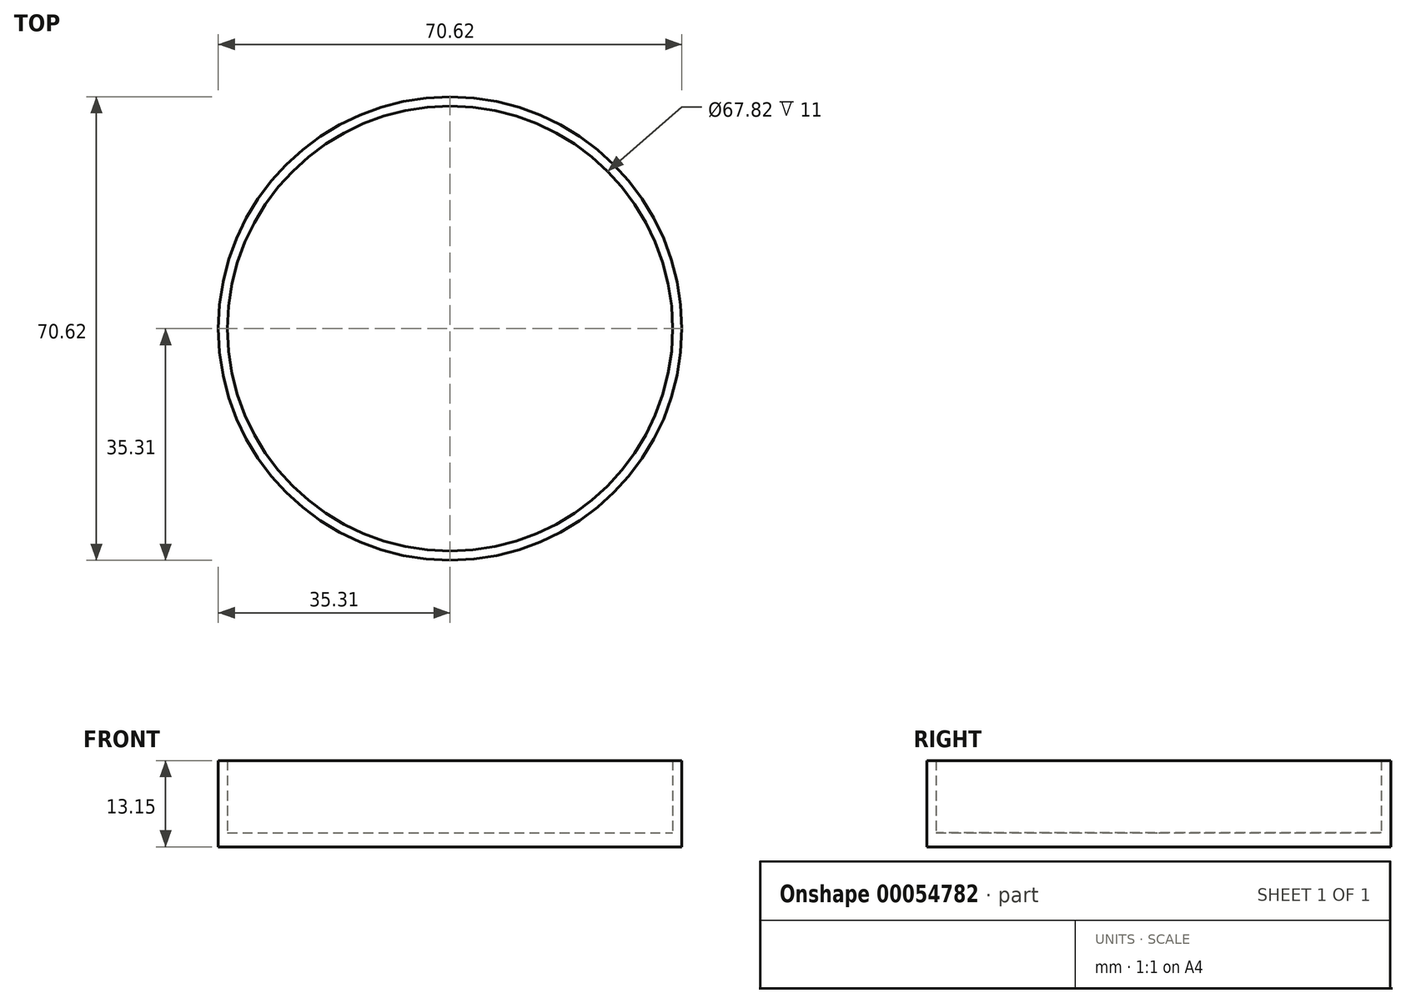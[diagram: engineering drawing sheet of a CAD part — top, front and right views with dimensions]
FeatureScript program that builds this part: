
annotation { "Feature Type Name" : "Feature", "Feature Type Description" : "" }
export const myFeature = defineFeature(function(context is Context, id is Id, definition is map)
    precondition{}
    {
        {
            var Q0;
            Q0=qCreatedBy(makeId("Front.planeOp"),FACE);
            var sketch = newSketch(context, id + "F0", { "sketchPlane" : qUnion([Q0])});
            skLineSegment(sketch, "E0", {"start": v(33.9, 0) * mm, "end": v(33.9, 11) * mm});
            skLineSegment(sketch, "E1", {"start": v(33.9, 0) * mm, "end": v(0, 0) * mm});
            skLineSegment(sketch, "E2", {"start": v(0, 0) * mm, "end": v(0, -2.15) * mm});
            skLineSegment(sketch, "E3", {"start": v(0, -2.15) * mm, "end": v(34.9, -2.15) * mm});
            skLineSegment(sketch, "E4", {"start": v(34.9, -2.15) * mm, "end": v(34.9, 11) * mm});
            skLineSegment(sketch, "E5", {"start": v(33.9, 11) * mm, "end": v(34.9, 11) * mm});
            skLineSegment(sketch, "E6", {"start": v(0, 0) * mm, "end": v(0, 19.84) * mm, "construction": true});
            skSolve(sketch);
        }
        {
            var Q0;
            Q0 = qSketchRegion(id + "F0", true);
            var Q1;
            Q1=sQuery(id+"F0.wireOp",EDGE,"E6");
            revolve(context, id + "F1", {"entities" : qUnion([Q0]), "axis" : qUnion([Q1]), "revolveType" : RevolveType.FULL});
        }
        {
            var Q0;
            Q0=makeQuery(id+"F1.opRevolve","SWEPT_FACE",FACE,{"disambiguationData":[OSD([sQuery(id+"F0.wireOp",EDGE,"E3")])]});
            var sketch = newSketch(context, id + "F2", { "sketchPlane" : qUnion([Q0])});
            skCircle(sketch, "E7", {"center": v(0, 0) * mm, "radius": 35.3 * mm});
            skCircle(sketch, "E8.0", {"center": v(0, 0) * mm, "radius": 34.9 * mm});
            skSolve(sketch);
        }
        {
            var Q0;
            Q0=makeQuery(id+"F2.imprint","IMPRINT",FACE,{"disambiguationData":[TD([[makeQuery(id+"F2.imprint","IMPRINT",EDGE,{"derivedFrom":sQuery(id+"F2.wireOp",EDGE,"E7")}),1.0]])]});
            var Q1;
            Q1=makeQuery(id+"F1.opRevolve","SWEPT_FACE",FACE,{"disambiguationData":[OSD([sQuery(id+"F0.wireOp",EDGE,"E5")])]});
            extrude(context, id + "F3", {"entities" : qUnion([Q0]), "operationType" : NewBodyOperationType.ADD, "endBound" : BoundingType.UP_TO_SURFACE, "oppositeDirection" : true, "endBoundEntityFace" : qUnion([Q1]), "depth" : 25 * mm});
        }
    });
